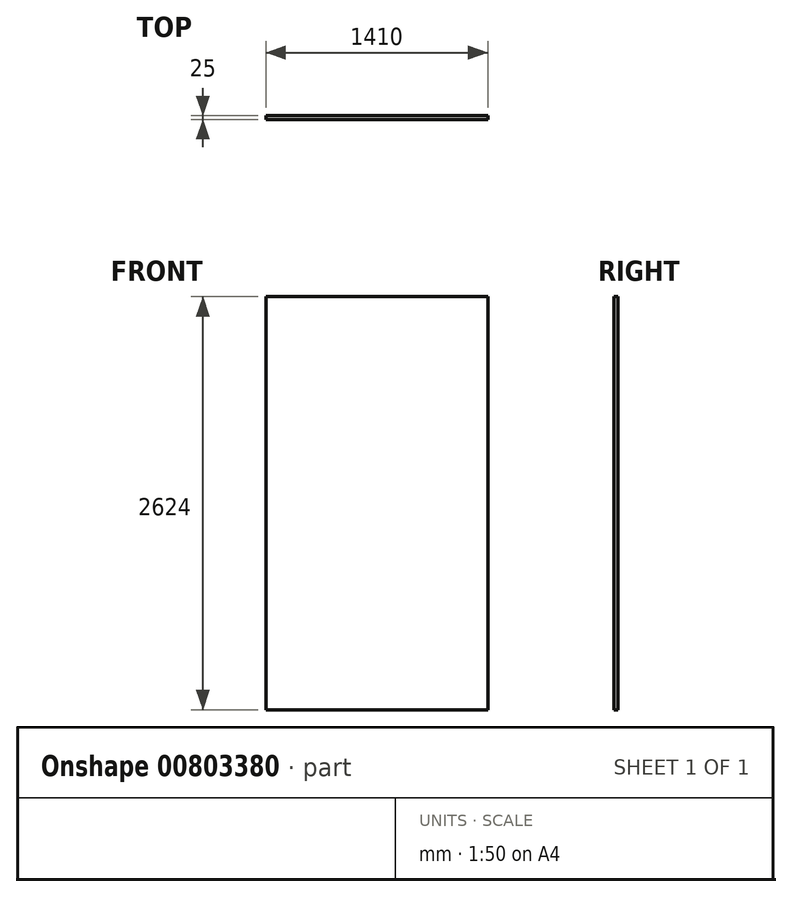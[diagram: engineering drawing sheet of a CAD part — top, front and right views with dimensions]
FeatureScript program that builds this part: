
annotation { "Feature Type Name" : "Feature", "Feature Type Description" : "" }
export const myFeature = defineFeature(function(context is Context, id is Id, definition is map)
    precondition{}
    {
        {
            var Q0;
            Q0=qCreatedBy(makeId("Front.planeOp"),FACE);
            var sketch = newSketch(context, id + "F0", { "sketchPlane" : qUnion([Q0])});
            skLineSegment(sketch, "E0.bottom", {"start": v(0, 0) * mm, "end": v(1410, 0) * mm});
            skLineSegment(sketch, "E0.top", {"start": v(0, -2624) * mm, "end": v(1410, -2624) * mm});
            skLineSegment(sketch, "E0.left", {"start": v(0, 0) * mm, "end": v(0, -2624) * mm});
            skLineSegment(sketch, "E0.right", {"start": v(1410, 0) * mm, "end": v(1410, -2624) * mm});
            skSolve(sketch);
        }
        {
            var Q0;
            Q0=makeQuery(id+"F0.imprint","IMPRINT",FACE,{"disambiguationData":[TD([[makeQuery(id+"F0.imprint","IMPRINT",EDGE,{"derivedFrom":sQuery(id+"F0.wireOp",EDGE,"E0.bottom")}),-1.0]])]});
            extrude(context, id + "F1", {"entities" : qUnion([Q0]), "depth" : 25 * mm, "offsetDistance" : 25 * mm});
        }
    });
